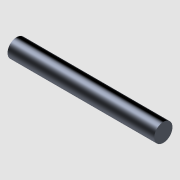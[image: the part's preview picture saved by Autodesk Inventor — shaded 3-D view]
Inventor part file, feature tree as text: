
AUTODESK INVENTOR PART (.ipt)
format: ipt  version: 2021 (Build 250183000, 183)  size: 105,472 bytes
history: native  units: in
note: dims shown in document units (in); Inventor stores cm internally (conversion verified against a paired STEP export)
features: extrude x2, other x1, imported_body x1, sketch x1
ambient origin geometry x8: Origin, YZ Plane, XZ Plane, XY Plane, X Axis, Y Axis, Z Axis, Center Point
bodies: Body1 (feature_tree)
feature tree (5):
  other  "Pin"
  extrude  "Extrude1"  TaperAngle=0.0deg  [1 undecoded]
  extrude  "Extrusion1"  [1 undecoded]
  imported_body  "Base1"
  sketch  "Sketch1"  dims[d1=1.5in d2=0.0in]
note: 2 required parameter values undecoded (feature->parameter linkage not recoverable at this tier; creation-order binding heuristic only, values carry confidence <= 0.55)
